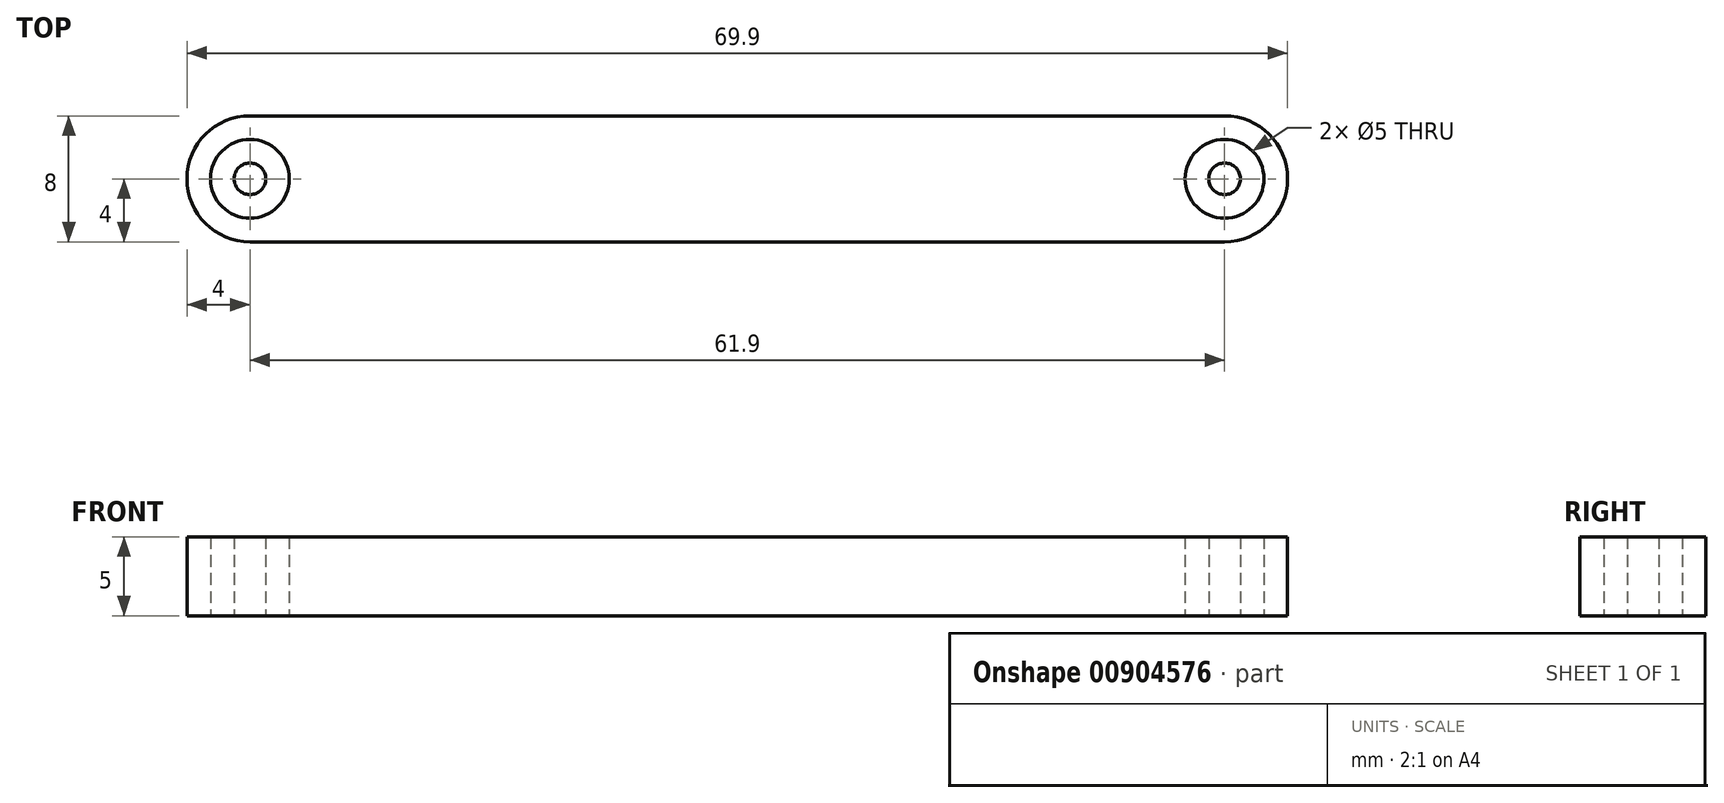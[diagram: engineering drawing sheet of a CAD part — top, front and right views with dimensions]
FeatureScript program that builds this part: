
annotation { "Feature Type Name" : "Feature", "Feature Type Description" : "" }
export const myFeature = defineFeature(function(context is Context, id is Id, definition is map)
    precondition{}
    {
        {
            var Q0;
            Q0=qCreatedBy(makeId("Top.planeOp"),FACE);
            var sketch = newSketch(context, id + "F0", { "sketchPlane" : qUnion([Q0])});
            skCircle(sketch, "E0", {"center": v(0, 0) * mm, "radius": 2.5 * mm});
            skCircle(sketch, "E1", {"center": v(61.9, 0) * mm, "radius": 2.5 * mm});
            skCircle(sketch, "E2", {"center": v(0, 0) * mm, "radius": 1 * mm});
            skCircle(sketch, "E3", {"center": v(61.9, 0) * mm, "radius": 1 * mm});
            skArc(sketch, "E4", {"start": v(0, 4) * mm, "mid": v(-4, 0) * mm, "end": v(0, -4) * mm});
            skArc(sketch, "E5", {"start": v(61.9, -4) * mm, "mid": v(65.9, 0) * mm, "end": v(61.9, 4) * mm});
            skLineSegment(sketch, "E6", {"start": v(0, 4) * mm, "end": v(61.9, 4) * mm});
            skLineSegment(sketch, "E7", {"start": v(0, -4) * mm, "end": v(61.9, -4) * mm});
            skSolve(sketch);
        }
        {
            var Q0;
            Q0=qSketchRegion(id+"F0",true);
            var Q1;
            Q1=makeQuery(id+"F0.imprint","IMPRINT",FACE,{"disambiguationData":[TD([[makeQuery(id+"F0.imprint","IMPRINT",EDGE,{"derivedFrom":sQuery(id+"F0.wireOp",EDGE,"E2")}),1.0]])]});
            var Q2;
            Q2=makeQuery(id+"F0.imprint","IMPRINT",FACE,{"disambiguationData":[TD([[makeQuery(id+"F0.imprint","IMPRINT",EDGE,{"derivedFrom":sQuery(id+"F0.wireOp",EDGE,"E3")}),1.0]])]});
            extrude(context, id + "F1", {"entities" : qUnion([Q0, Q1, Q2]), "endBound" : BoundingType.SYMMETRIC, "depth" : 5 * mm, "offsetDistance" : 25.4 * mm});
        }
    });
